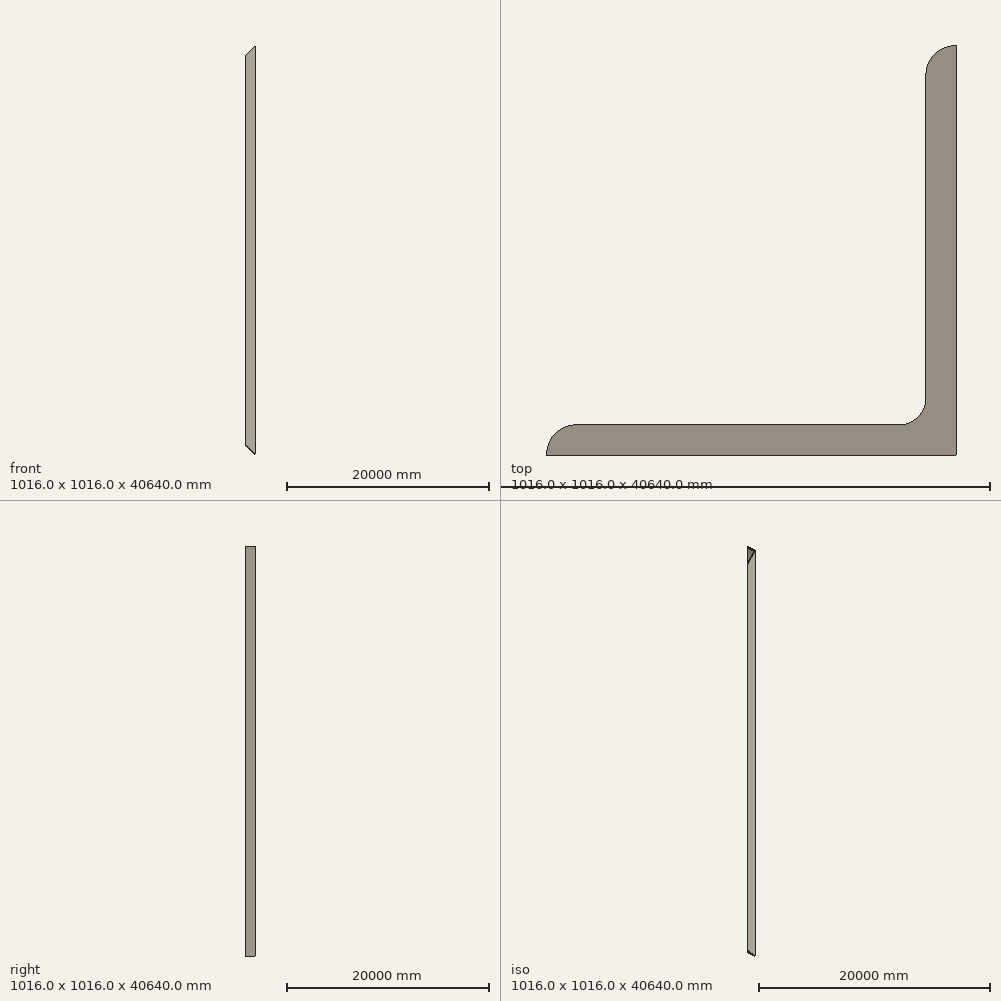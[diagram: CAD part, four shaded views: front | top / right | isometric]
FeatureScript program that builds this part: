
annotation { "Feature Type Name" : "Feature", "Feature Type Description" : "" }
export const myFeature = defineFeature(function(context is Context, id is Id, definition is map)
    precondition{}
    {
        {
            var Q0;
            Q0=qCreatedBy(makeId("Top.planeOp"),FACE);
            var sketch = newSketch(context, id + "F0", { "sketchPlane" : qUnion([Q0])});
            skLineSegment(sketch, "E0", {"start": v(0, 0) * mm, "end": v(1016, 0) * mm});
            skLineSegment(sketch, "E1", {"start": v(1016, 0) * mm, "end": v(1016, 1016) * mm});
            skLineSegment(sketch, "E2", {"start": v(939.8, 939.8) * mm, "end": v(939.8, 139.7) * mm});
            skLineSegment(sketch, "E3", {"start": v(876.3, 76.2) * mm, "end": v(76.2, 76.2) * mm});
            skArc(sketch, "E4", {"start": v(0, 0) * mm, "mid": v(22.32, 53.88) * mm, "end": v(76.2, 76.2) * mm});
            skArc(sketch, "E5", {"start": v(939.8, 939.8) * mm, "mid": v(962.12, 993.68) * mm, "end": v(1016, 1016) * mm});
            skPoint(sketch, "E6.visualSharp", {"position": v(939.8, 76.2) * mm});
            skArc(sketch, "E6.filletArc", {"start": v(876.3, 76.2) * mm, "mid": v(921.2, 94.8) * mm, "end": v(939.8, 139.7) * mm});
            skSolve(sketch);
        }
        {
            var Q0;
            Q0 = qSketchRegion(id + "F0", true);
            extrude(context, id + "F1", {"entities" : qUnion([Q0]), "depth" : 40640 * mm, "offsetDistance" : 25.4 * mm});
        }
        {
            var Q0;
            Q0=makeQuery(id+"F1.opExtrude","SWEPT_FACE",FACE,{"disambiguationData":[OSD([sQuery(id+"F0.wireOp",EDGE,"E0")])]});
            var sketch = newSketch(context, id + "F2", { "sketchPlane" : qUnion([Q0])});
            skLineSegment(sketch, "E7", {"start": v(1016, 40640) * mm, "end": v(-164.11, 39459.89) * mm});
            skLineSegment(sketch, "E8", {"start": v(-164.11, 39459.89) * mm, "end": v(-279.23, 40837.4) * mm});
            skLineSegment(sketch, "E9", {"start": v(-279.23, 40837.4) * mm, "end": v(1016, 40640) * mm});
            skLineSegment(sketch, "E10", {"start": v(1016, 0) * mm, "end": v(-327.48, 1343.48) * mm});
            skLineSegment(sketch, "E11", {"start": v(-327.48, 1343.48) * mm, "end": v(-240.69, -519.2) * mm});
            skLineSegment(sketch, "E12", {"start": v(-240.69, -519.2) * mm, "end": v(1016, 0) * mm});
            skSolve(sketch);
        }
        {
            var Q0;
            {var subQ1=sQuery(id+"F0.wireOp",EDGE,"E0");var subQ2=makeQuery(id+"F1.opExtrude","CAP_EDGE",EDGE,{"disambiguationData":[OSD([subQ1])],"isStart":true});Q0=makeQuery(id+"F2.imprint","IMPRINT",FACE,{"disambiguationData":[TD([[makeQuery(id+"F2.imprint","IMPRINT",EDGE,{"derivedFrom":subQ2}),1.0]])]});}
            var Q1;
            {var subQ1=sQuery(id+"F0.wireOp",EDGE,"E0");var subQ2=makeQuery(id+"F1.opExtrude","CAP_EDGE",EDGE,{"disambiguationData":[OSD([subQ1])],"isStart":false});Q1=makeQuery(id+"F2.imprint","IMPRINT",FACE,{"disambiguationData":[TD([[makeQuery(id+"F2.imprint","IMPRINT",EDGE,{"derivedFrom":subQ2}),-1.0]])]});}
            extrude(context, id + "F3", {"entities" : qUnion([Q0, Q1]), "operationType" : NewBodyOperationType.REMOVE, "endBound" : BoundingType.THROUGH_ALL, "oppositeDirection" : true, "depth" : 25.4 * mm, "offsetDistance" : 25.4 * mm});
        }
    });
